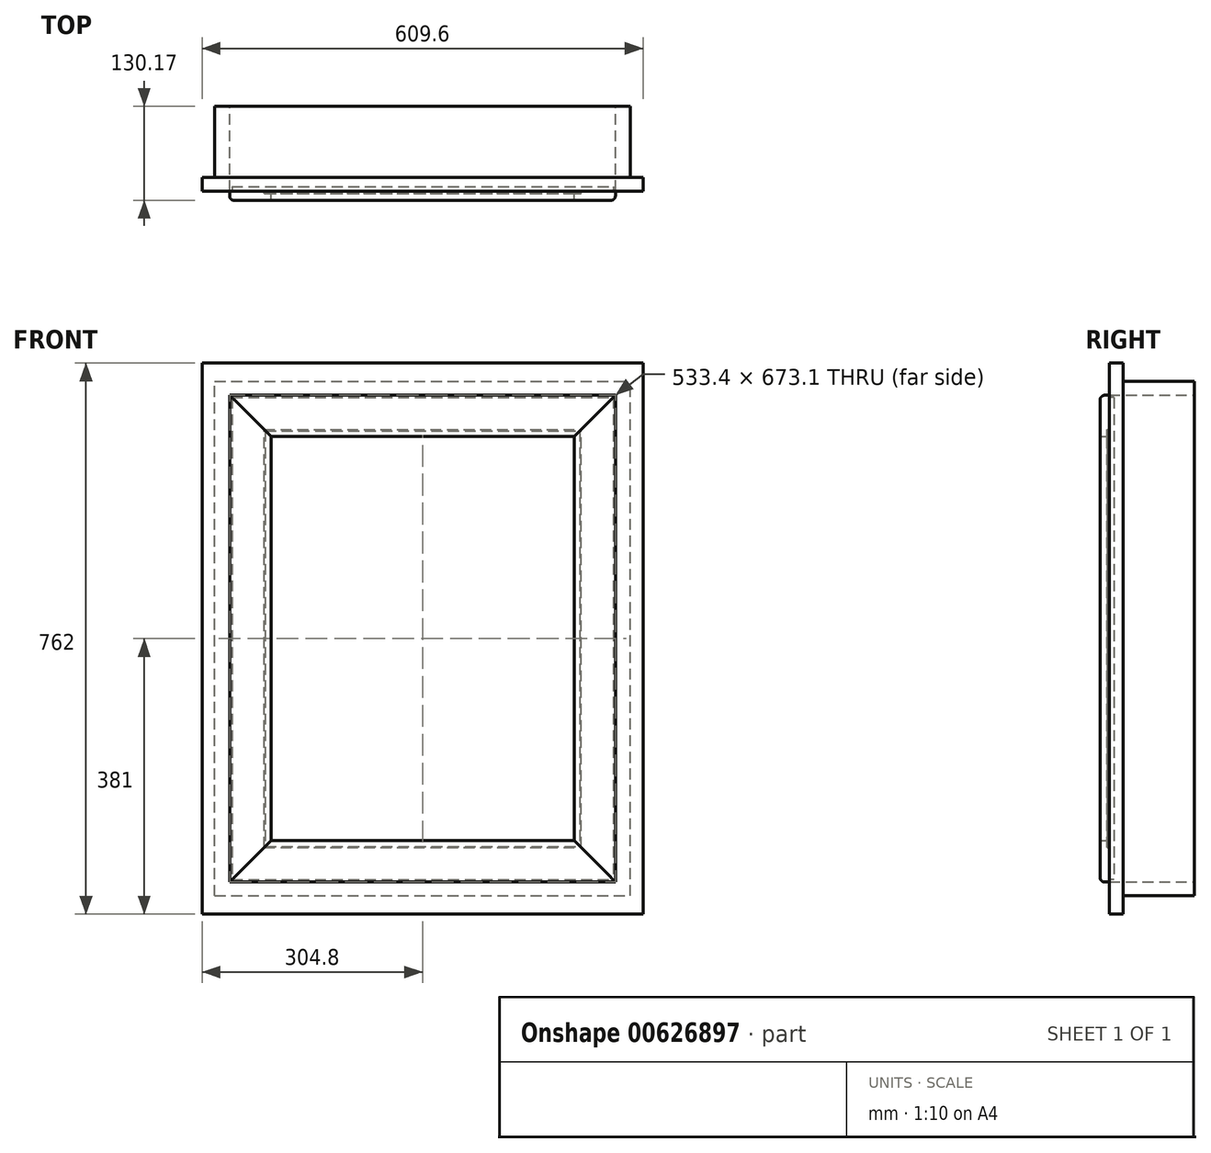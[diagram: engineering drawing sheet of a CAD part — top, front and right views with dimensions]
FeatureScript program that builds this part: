
annotation { "Feature Type Name" : "Feature", "Feature Type Description" : "" }
export const myFeature = defineFeature(function(context is Context, id is Id, definition is map)
    precondition{}
    {
        {
            var Q0;
            Q0=qCreatedBy(makeId("Front.planeOp"),FACE);
            var sketch = newSketch(context, id + "F0", { "sketchPlane" : qUnion([Q0])});
            skLineSegment(sketch, "E0.bottom", {"start": v(304.8, 381) * mm, "end": v(-304.8, 381) * mm});
            skLineSegment(sketch, "E0.top", {"start": v(304.8, -381) * mm, "end": v(-304.8, -381) * mm});
            skLineSegment(sketch, "E0.left", {"start": v(304.8, 381) * mm, "end": v(304.8, -381) * mm});
            skLineSegment(sketch, "E0.right", {"start": v(-304.8, 381) * mm, "end": v(-304.8, -381) * mm});
            skPoint(sketch, "E0.middle", {"position": v(0, 0) * mm});
            skLineSegment(sketch, "E1.bottom", {"start": v(266.7, -336.55) * mm, "end": v(-266.7, -336.55) * mm});
            skLineSegment(sketch, "E1.top", {"start": v(266.7, 336.55) * mm, "end": v(-266.7, 336.55) * mm});
            skLineSegment(sketch, "E1.left", {"start": v(266.7, -336.55) * mm, "end": v(266.7, 336.55) * mm});
            skLineSegment(sketch, "E1.right", {"start": v(-266.7, -336.55) * mm, "end": v(-266.7, 336.55) * mm});
            skSolve(sketch);
        }
        {
            var Q0;
            Q0=makeQuery(id+"F0.imprint","IMPRINT",FACE,{"disambiguationData":[TD([[makeQuery(id+"F0.imprint","IMPRINT",EDGE,{"derivedFrom":sQuery(id+"F0.wireOp",EDGE,"E0.bottom")}),1.0]])]});
            extrude(context, id + "F1", {"entities" : qUnion([Q0]), "depth" : 19.05 * mm, "offsetDistance" : 25.4 * mm});
        }
        {
            var Q0;
            Q0=makeQuery(id+"F1.opExtrude","CAP_FACE",FACE,{"disambiguationData":[OSD([sQuery(id+"F0.wireOp",EDGE,"E0.bottom"),sQuery(id+"F0.wireOp",EDGE,"E0.top"),sQuery(id+"F0.wireOp",EDGE,"E0.left"),sQuery(id+"F0.wireOp",EDGE,"E0.right"),sQuery(id+"F0.wireOp",EDGE,"E1.bottom"),sQuery(id+"F0.wireOp",EDGE,"E1.top"),sQuery(id+"F0.wireOp",EDGE,"E1.left"),sQuery(id+"F0.wireOp",EDGE,"E1.right")])],"isStart":true});
            var sketch = newSketch(context, id + "F2", { "sketchPlane" : qUnion([Q0])});
            skLineSegment(sketch, "E2.bottom", {"start": v(287.34, -355.6) * mm, "end": v(-287.34, -355.6) * mm});
            skLineSegment(sketch, "E2.top", {"start": v(287.34, 355.6) * mm, "end": v(-287.34, 355.6) * mm});
            skLineSegment(sketch, "E2.left", {"start": v(287.34, -355.6) * mm, "end": v(287.34, 355.6) * mm});
            skLineSegment(sketch, "E2.right", {"start": v(-287.34, -355.6) * mm, "end": v(-287.34, 355.6) * mm});
            skPoint(sketch, "E2.middle", {"position": v(0, 0) * mm});
            skLineSegment(sketch, "E3.bottom", {"start": v(266.7, 336.55) * mm, "end": v(-266.7, 336.55) * mm});
            skLineSegment(sketch, "E3.top", {"start": v(266.7, -336.55) * mm, "end": v(-266.7, -336.55) * mm});
            skLineSegment(sketch, "E3.left", {"start": v(266.7, 336.55) * mm, "end": v(266.7, -336.55) * mm});
            skLineSegment(sketch, "E3.right", {"start": v(-266.7, 336.55) * mm, "end": v(-266.7, -336.55) * mm});
            skSolve(sketch);
        }
        {
            var Q0;
            Q0 = qSketchRegion(id + "F2", true);
            extrude(context, id + "F3", {"entities" : qUnion([Q0]), "operationType" : NewBodyOperationType.ADD, "depth" : 98.42 * mm, "offsetDistance" : 25.4 * mm});
        }
        {
            var Q0;
            Q0=makeQuery(id+"F1.opExtrude","CAP_FACE",FACE,{"disambiguationData":[OSD([sQuery(id+"F0.wireOp",EDGE,"E0.bottom"),sQuery(id+"F0.wireOp",EDGE,"E0.top"),sQuery(id+"F0.wireOp",EDGE,"E0.left"),sQuery(id+"F0.wireOp",EDGE,"E0.right"),sQuery(id+"F0.wireOp",EDGE,"E1.bottom"),sQuery(id+"F0.wireOp",EDGE,"E1.top"),sQuery(id+"F0.wireOp",EDGE,"E1.left"),sQuery(id+"F0.wireOp",EDGE,"E1.right")])],"isStart":false});
            var sketch = newSketch(context, id + "F4", { "sketchPlane" : qUnion([Q0])});
            skLineSegment(sketch, "E4.top", {"start": v(273.05, 342.9) * mm, "end": v(-273.05, 342.9) * mm});
            skLineSegment(sketch, "E4.right", {"start": v(-273.05, -342.9) * mm, "end": v(-273.05, 342.9) * mm, "construction": true});
            skPoint(sketch, "E4.middle", {"position": v(0, 0) * mm});
            skLineSegment(sketch, "E5", {"start": v(-273.05, 342.9) * mm, "end": v(-209.55, 279.4) * mm});
            skLineSegment(sketch, "E6", {"start": v(273.05, 342.9) * mm, "end": v(209.55, 279.4) * mm});
            skLineSegment(sketch, "E7", {"start": v(-209.55, 279.4) * mm, "end": v(209.55, 279.4) * mm});
            skLineSegment(sketch, "E8", {"start": v(266.7, 0) * mm, "end": v(-273.05, 0) * mm, "construction": true});
            skLineSegment(sketch, "E9.MirrorCS", {"start": v(-273.05, -342.9) * mm, "end": v(-209.55, -279.4) * mm});
            skLineSegment(sketch, "E10", {"start": v(-273.05, -342.9) * mm, "end": v(-273.05, 342.9) * mm});
            skLineSegment(sketch, "E11", {"start": v(-209.55, -279.4) * mm, "end": v(-209.55, 279.4) * mm});
            skSolve(sketch);
        }
        {
            var Q0;
            {var subQ2=sQuery(id+"F4.wireOp",EDGE,"E7");Q0=makeQuery(id+"F4.imprint","IMPRINT",FACE,{"disambiguationData":[TD([[makeQuery(id+"F4.imprint","IMPRINT",EDGE,{"derivedFrom":subQ2}),1.0]])]});}
            var Q1;
            {var subQ2=sQuery(id+"F4.wireOp",EDGE,"82c725d1-780c-4a3b-bc1a-e1fffcf4e3860.MirrorCS");Q1=makeQuery(id+"F4.imprint","IMPRINT",FACE,{"disambiguationData":[TD([[makeQuery(id+"F4.imprint","IMPRINT",EDGE,{"derivedFrom":subQ2}),-1.0]])]});}
            extrude(context, id + "F5", {"entities" : qUnion([Q0, Q1]), "depth" : 12.7 * mm, "offsetDistance" : 25.4 * mm});
        }
        {
            var Q0;
            {var subQ2=sQuery(id+"F4.wireOp",EDGE,"E11");Q0=makeQuery(id+"F4.imprint","IMPRINT",FACE,{"disambiguationData":[TD([[makeQuery(id+"F4.imprint","IMPRINT",EDGE,{"derivedFrom":subQ2}),1.0]])]});}
            var Q1;
            {var subQ2=sQuery(id+"F4.wireOp",EDGE,"TzazxIpp-MqKM-UETf-3Omg-7LUC9r8btUxf");Q1=makeQuery(id+"F4.imprint","IMPRINT",FACE,{"disambiguationData":[TD([[makeQuery(id+"F4.imprint","IMPRINT",EDGE,{"derivedFrom":subQ2}),-1.0]])]});}
            extrude(context, id + "F6", {"entities" : qUnion([Q0, Q1]), "depth" : 12.7 * mm, "offsetDistance" : 25.4 * mm});
        }
        {
            var Q0;
            Q0=makeQuery(id+"F5.opExtrude","CAP_EDGE",EDGE,{"disambiguationData":[OSD([sQuery(id+"F0.wireOp",EDGE,"E1.top")])],"isStart":false});
            var Q1;
            Q1=makeQuery(id+"F6.opExtrude","CAP_EDGE",EDGE,{"disambiguationData":[OSD([sQuery(id+"F0.wireOp",EDGE,"E1.right")])],"isStart":false});
            var Q2;
            Q2=makeQuery(id+"F6.opExtrude","CAP_EDGE",EDGE,{"disambiguationData":[OSD([sQuery(id+"F0.wireOp",EDGE,"E1.left")])],"isStart":false});
            var Q3;
            Q3=makeQuery(id+"F5.opExtrude","CAP_EDGE",EDGE,{"disambiguationData":[OSD([sQuery(id+"F0.wireOp",EDGE,"E1.bottom")])],"isStart":false});
            fillet(context, id + "F7", {"entities" : qUnion([Q0, Q1, Q2, Q3]), "radius" : 6.35 * mm, "tangentPropagation" : true, "allowEdgeOverflow" : false});
        }
        {
            var Q0;
            Q0=makeQuery(id+"F5.opExtrude","CAP_FACE",FACE,{"disambiguationData":[OSD([sQuery(id+"F0.wireOp",EDGE,"E1.top"),sQuery(id+"F4.wireOp",EDGE,"E5"),sQuery(id+"F4.wireOp",EDGE,"E6"),sQuery(id+"F4.wireOp",EDGE,"E7")])],"isStart":true});
            var sketch = newSketch(context, id + "F8", { "sketchPlane" : qUnion([Q0])});
            skLineSegment(sketch, "E12.bottom", {"start": v(219.08, 269.88) * mm, "end": v(-219.08, 269.88) * mm});
            skLineSegment(sketch, "E12.top", {"start": v(219.08, 288.93) * mm, "end": v(-219.08, 288.93) * mm});
            skLineSegment(sketch, "E12.left", {"start": v(219.08, 269.88) * mm, "end": v(219.08, 288.93) * mm});
            skLineSegment(sketch, "E12.right", {"start": v(-219.08, 269.88) * mm, "end": v(-219.08, 288.93) * mm});
            skPoint(sketch, "E12.middle", {"position": v(0, 279.4) * mm});
            skPoint(sketch, "E13", {"position": v(209.55, 279.4) * mm});
            skSolve(sketch);
        }
        {
            var Q0;
            Q0 = qSketchRegion(id + "F8", true);
            extrude(context, id + "F9", {"entities" : qUnion([Q0]), "operationType" : NewBodyOperationType.REMOVE, "oppositeDirection" : true, "depth" : 3.17 * mm, "offsetDistance" : 25.4 * mm});
        }
        {
            var Q0;
            Q0=makeQuery(id+"F6.opExtrude","CAP_FACE",FACE,{"disambiguationData":[OSD([sQuery(id+"F0.wireOp",EDGE,"E1.right"),sQuery(id+"F4.wireOp",EDGE,"E5"),sQuery(id+"F4.wireOp",EDGE,"E9.MirrorCS"),sQuery(id+"F4.wireOp",EDGE,"E11")])],"isStart":true});
            var sketch = newSketch(context, id + "F10", { "sketchPlane" : qUnion([Q0])});
            skLineSegment(sketch, "E14.bottom", {"start": v(219.08, 288.93) * mm, "end": v(200.03, 288.93) * mm});
            skLineSegment(sketch, "E14.top", {"start": v(219.08, -288.93) * mm, "end": v(200.03, -288.93) * mm});
            skLineSegment(sketch, "E14.left", {"start": v(219.08, 288.93) * mm, "end": v(219.08, -288.93) * mm});
            skLineSegment(sketch, "E14.right", {"start": v(200.03, 288.93) * mm, "end": v(200.03, -288.93) * mm});
            skPoint(sketch, "E14.middle", {"position": v(209.55, 0) * mm});
            skSolve(sketch);
        }
        {
            var Q0;
            Q0 = qSketchRegion(id + "F10", true);
            extrude(context, id + "F11", {"entities" : qUnion([Q0]), "operationType" : NewBodyOperationType.REMOVE, "oppositeDirection" : true, "depth" : 3.17 * mm, "offsetDistance" : 25.4 * mm});
        }
        {
            var Q0;
            Q0=makeQuery(id+"F6.opExtrude","SWEPT_BODY",BODY,{"disambiguationData":[OSD([sQuery(id+"F0.wireOp",EDGE,"E1.right"),sQuery(id+"F4.wireOp",EDGE,"E5"),sQuery(id+"F4.wireOp",EDGE,"E9.MirrorCS"),sQuery(id+"F4.wireOp",EDGE,"E11")])]});
            var Q1;
            Q1=qCreatedBy(makeId("Right.planeOp"),FACE);
            mirror(context, id + "F12", {"entities" : qUnion([Q0]), "mirrorPlane" : qUnion([Q1])});
        }
        {
            var Q0;
            Q0=makeQuery(id+"F5.opExtrude","SWEPT_BODY",BODY,{"disambiguationData":[OSD([sQuery(id+"F0.wireOp",EDGE,"E1.top"),sQuery(id+"F4.wireOp",EDGE,"E5"),sQuery(id+"F4.wireOp",EDGE,"E6"),sQuery(id+"F4.wireOp",EDGE,"E7")])]});
            var Q1;
            Q1=qCreatedBy(makeId("Top.planeOp"),FACE);
            mirror(context, id + "F13", {"entities" : qUnion([Q0]), "mirrorPlane" : qUnion([Q1])});
        }
        {
            var Q0;
            Q0=makeQuery(id+"F9.boolean.opBoolean","COPY",FACE,{"derivedFrom":makeQuery(id+"F9.opExtrude","CAP_FACE",FACE,{"disambiguationData":[OSD([sQuery(id+"F8.wireOp",EDGE,"E12.bottom"),sQuery(id+"F8.wireOp",EDGE,"E12.top"),sQuery(id+"F8.wireOp",EDGE,"E12.left"),sQuery(id+"F8.wireOp",EDGE,"E12.right")])],"isStart":false})});
            var sketch = newSketch(context, id + "F14", { "sketchPlane" : qUnion([Q0])});
            skLineSegment(sketch, "E15.bottom", {"start": v(217.49, 287.34) * mm, "end": v(-217.49, 287.34) * mm});
            skLineSegment(sketch, "E15.top", {"start": v(217.49, -287.34) * mm, "end": v(-217.49, -287.34) * mm});
            skLineSegment(sketch, "E15.left", {"start": v(217.49, 287.34) * mm, "end": v(217.49, -287.34) * mm});
            skLineSegment(sketch, "E15.right", {"start": v(-217.49, 287.34) * mm, "end": v(-217.49, -287.34) * mm});
            skPoint(sketch, "E15.middle", {"position": v(0, 0) * mm});
            skSolve(sketch);
        }
        {
            var Q0;
            Q0 = qSketchRegion(id + "F14", true);
            extrude(context, id + "F15", {"entities" : qUnion([Q0]), "depth" : 3.17 * mm, "offsetDistance" : 25.4 * mm});
        }
        {
            var Q0;
            Q0=makeQuery(id+"F15.opExtrude","CAP_FACE",FACE,{"disambiguationData":[OSD([sQuery(id+"F14.wireOp",EDGE,"E15.bottom"),sQuery(id+"F14.wireOp",EDGE,"E15.top"),sQuery(id+"F14.wireOp",EDGE,"E15.left"),sQuery(id+"F14.wireOp",EDGE,"E15.right")])],"isStart":false});
            var sketch = newSketch(context, id + "F16", { "sketchPlane" : qUnion([Q0])});
            skLineSegment(sketch, "E16.bottom", {"start": v(265.11, -334.96) * mm, "end": v(-265.11, -334.96) * mm});
            skLineSegment(sketch, "E16.top", {"start": v(265.11, 334.96) * mm, "end": v(-265.11, 334.96) * mm});
            skLineSegment(sketch, "E16.left", {"start": v(265.11, -334.96) * mm, "end": v(265.11, 334.96) * mm});
            skLineSegment(sketch, "E16.right", {"start": v(-265.11, -334.96) * mm, "end": v(-265.11, 334.96) * mm});
            skPoint(sketch, "E16.middle", {"position": v(0, 0) * mm});
            skSolve(sketch);
        }
        {
            var Q0;
            Q0 = qSketchRegion(id + "F16", true);
            extrude(context, id + "F17", {"entities" : qUnion([Q0]), "depth" : 6.35 * mm, "offsetDistance" : 25.4 * mm});
        }
        {
            var Q0;
            Q0=makeQuery(id+"F5.opExtrude","CAP_FACE",FACE,{"disambiguationData":[OSD([sQuery(id+"F0.wireOp",EDGE,"E1.top"),sQuery(id+"F4.wireOp",EDGE,"E5"),sQuery(id+"F4.wireOp",EDGE,"E6"),sQuery(id+"F4.wireOp",EDGE,"E7")])],"isStart":true});
            var sketch = newSketch(context, id + "F18", { "sketchPlane" : qUnion([Q0])});
            skLineSegment(sketch, "E17.bottom", {"start": v(263.53, 333.38) * mm, "end": v(-263.53, 333.38) * mm});
            skLineSegment(sketch, "E17.top", {"start": v(263.53, -333.38) * mm, "end": v(-263.53, -333.38) * mm});
            skLineSegment(sketch, "E17.left", {"start": v(263.53, 333.38) * mm, "end": v(263.53, -333.38) * mm});
            skLineSegment(sketch, "E17.right", {"start": v(-263.53, 333.38) * mm, "end": v(-263.53, -333.38) * mm});
            skPoint(sketch, "E17.middle", {"position": v(0, 0) * mm});
            skSolve(sketch);
        }
        {
            var Q0;
            Q0 = qSketchRegion(id + "F18", true);
            extrude(context, id + "F19", {"entities" : qUnion([Q0]), "depth" : 6.35 * mm, "offsetDistance" : 25.4 * mm});
        }
        {
            var Q0;
            Q0=makeQuery(id+"F17.opExtrude","SWEPT_BODY",BODY,{"disambiguationData":[OSD([sQuery(id+"F16.wireOp",EDGE,"E16.bottom"),sQuery(id+"F16.wireOp",EDGE,"E16.top"),sQuery(id+"F16.wireOp",EDGE,"E16.left"),sQuery(id+"F16.wireOp",EDGE,"E16.right")])]});
            deleteBodies(context, id + "F20", {"entities" : qUnion([Q0])});
        }
    });
